# Revit family: Shower-Valve_Trim-KOHLER-Purist-K-7356IN
name_source: partatom
category: Specialty Equipment
revit_build: Autodesk Revit 2017 (Build: 20160225_1515(x64)
units: mm (PartAtom-declared; Revit-internal decimal feet)

## family parameters
Cut with Voids When Loaded = No
Host = Face
OmniClass Number = 23.31.25.00
OmniClass Title = Toilet and Bath Specialties
Part Type = Normal
Room Calculation Point = No
Round Connector Dimension = Use Diameter
Shared = No

## types (5) — shared parameters
ADA Compliant = No
Assembly Code = C1030200
Date Modified = 09/15/2020
Default Elevation = 42"
Height = 6 15/16"
Length = 4 1/4"
Manufacturer = KOHLER Co.
Master Format 2014 = 10 28 00
Master Format 2014 Name = Toilet, Bath, and Laundry Accessories
Material = Premium Metal Construction
Product Name = Purist
URL = https://www.kohler.co.in
WaterSense Certified = No
Width = 6 15/16"

## per-type parameters (varying)
| type | Description | Finish | Model | Product Documentation Link | Product Page URL | Type |
| CP-Polished Chrome | Single Lever Recessed Trim | Kohler-Metal-CP-Polished_Chrome | K-7356IN-4-CP |  |  | 1 |
| BGD-Brushed Gold | Single Lever Recessed Trim | Kohler-Metal-BGD-Vibrant_Moderne_Brushed_Gold | K-7356IN-4-BGD |  |  | 2 |
| PGD-Polished Gold | Single Lever Recessed Trim | Kohler-Metal-PGD-Modern_Polished_Gold | K-7356IN-4-PGD |  |  | 3 |
| RGD-Rose Gold | Single Lever Recessed Trim | Kohler-Metal-RGD-Polished_Rose_Gold | K-7356IN-4-RGD |  |  | 4 |
| FP, CP-Polished Chrome | Recessed bath and shower faucet trim with lever handle and diverter button | Kohler-Metal-CP-Polished_Chrome | K-7356IN-4FP-CP | http://resources.kohler.com | https://www.kohler.co.in | 5 |

## geometry (parser evidence)
native form markers: Sweep x6
no freeform markers — native parametric forms only
